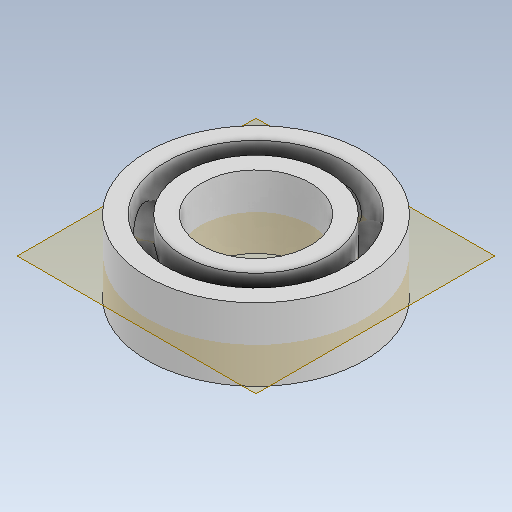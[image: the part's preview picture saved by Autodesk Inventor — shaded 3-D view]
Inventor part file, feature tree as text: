
AUTODESK INVENTOR PART (.ipt)
format: ipt  version: 2023 (Build 270158000, 158)  size: 226,816 bytes
history: native  units: mm
features: other x3, sketch x3, plane x1
ambient origin geometry x8: Origin, YZ Plane, XZ Plane, XY Plane, X Axis, Y Axis, Z Axis, Center Point
bodies: Solid1 (feature_tree)
feature tree (7):
  other  "bearing_3_6_2.ipt"
  other  "Solid1::bearing_3_6_2.ipt"
  other  "TaggingFeature1"
  sketch  "Sketch1"  dims[d0=10.0mm]
  sketch  "Sketch2"
  sketch  "Sketch3"
  plane  "Work Plane1"
